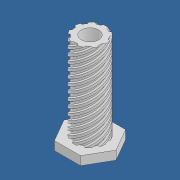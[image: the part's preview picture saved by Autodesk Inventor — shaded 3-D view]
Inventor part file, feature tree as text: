
AUTODESK INVENTOR PART (.ipt)
format: ipt  version: 2022.5 (Build 265521000, 521)  size: 700,416 bytes
history: native  units: mm
features: extrude x2, other x1, helix x1, pattern_circular x1, hole x1
ambient origin geometry x8: Origin, YZ Plane, XZ Plane, XY Plane, X Axis, Y Axis, Z Axis, Center Point
bodies: Body1 (feature_tree)
feature tree (6):
  other  "實體1"
  extrude  "擠出1"  Depth=10.0mm
  extrude  "擠出2"  Depth=90.0mm
  helix  "螺旋1"  [1 undecoded]
  pattern_circular  "環形陣列1"  Count=2  [1 undecoded]
  hole  "孔1"  [1 undecoded]
note: 3 required parameter values undecoded (feature->parameter linkage not recoverable at this tier; creation-order binding heuristic only, values carry confidence <= 0.55)
